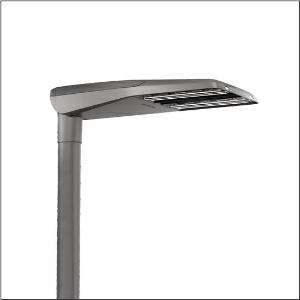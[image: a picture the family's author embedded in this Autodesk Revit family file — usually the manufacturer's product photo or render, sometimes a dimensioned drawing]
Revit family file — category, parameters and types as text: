
# Revit family: streetlight_sl_11_iq_midi___st1_0st0_5_5xc3j51g08me_56cc
name_source: partatom
category: Lighting Fixtures
units: mm (PartAtom-declared; Revit-internal decimal feet)

## family parameters
Cut with Voids When Loaded = No
Host = Face
Light Source = No
Part Type = Normal
Room Calculation Point = No
Round Connector Dimension = Use Diameter
Shared = No

## types (1)
- --- (1 x LED, 9460 lm, 63 W, 3000K)
    Apparent Load = 63 VA
    CIE Flux Codes = 35 68 96 100 100
    Color Rendering = 70
    Color Temperature = 3000K
    Default Elevation = 1800 mm
    Description = Streetlight SL 11 iQ midi, mast luminaire, primary light control with 3 zone facetted reflector, of plastic, silver coated, highly specular, primary optical cover: cover, of PMMA, transparent, light distribution: ST1.0ST0.5, light emission: direct distribution, primary light characteristic: asymmetric, installation type: post-top, side-entry, LED, High Power LED, rated luminous flux: 9.460lm, luminous efficacy: 150lm/W, light colour: 730, colour temperature: 3000K, control: Street-Remote, Auto-Match, Temp-Guard, Lumen-Switch, Night-Set, Smart-Wire, Light-Fading, Desk-Remote (wireless, voltage-free reading and setting of iQ features in the workshop via application-optimized NFC function/RFID function), optimised constant luminous flux control (CLO 2.0), pre-setting: linear dimming characteristic, with cable H07RN-F 5x 1.5mm², mains connection: 230..240V, AC, 50/60Hz, connection cable pre-assembled, cable length: 12,5m, start of lifetime: 63W, end of service life: 67W, reduction: 30W, luminaire housing, of diecast aluminium, powder-coated, Siteco® metallic grey (DB 702S), please order mast flange separately, inclination adjustable without tools: 0°, 5°, 10°, 15° (post-top) | 0°, -5°, -10°, -15° (side-entry), sealing non-destructively replaceable, multi-level sealing system, length: 780mm, width: 376mm, height: 118mm, mast flange for spigot size: 42mm (side-entry): 5XC10008XM4, 60/48mm (side-entry/post-top): 5XC10108XM2, 76/60mm (side-entry/post-top): 5XC10108XM1, equipment: Power, protection rating (complete): IP66, insulation class (complete): insulation class II (safety insulation), certification: CE, ENEC, VDE, impact resistance: IK09, permissible operating ambient temperature for outdoor applications: -25..+50°C, standard-compliant lighting for roads and squares, Environmental Product Declaration (EPD) tested and certified by an independent institute, packaging unit: 1 piece

Light Distribution: ST1.0ST0.5
    Height = 118 mm
    Lamp = 1 x LED
    Lamp Light Flux = 9460 lm
    Lamp Power = 63 W
    Lamp count = 1
    Length = 780 mm
    Luminous efficacy = 150 lm/W
    Manufacturer = Siteco
    ModVariant = No
    Model = 5XC3J51G08ME
    Number of Poles = 1
    OnlyDefault = Yes
    Power Factor = 1
    Product Name = Streetlight SL 11 iQ midi | ST1.0ST0.5
    Product group = mast luminaire | pylon top
    ProductGroupID = 6100
    Protection Class = Protection class II
    Protection Degree = IP 66
    RLX_Detail_Level = 1
    RLX_Emergency_Light_Flux = 0 lm
    RLX_Emergency_Type = 0
    RLX_Emergency_Type_DB = No
    RlxData = <blob elided: 70545 chars, md5=0e4ca75e>
    Socket = socket
    Standby Power = 0 W
    System Light Flux = 9460 lm
    System Power = 63 W
    Type Comments = factory setting: luminous flux: 100 % | dim-lin: 254 | 553 mA
    Type Image = l_1005960.jpg
    URL = http://relux.com
    VarID = @adj_008811
    Voltage = 0 V
    Weight = 0.00 kg
    Width = 376 mm

## geometry (parser evidence)
native form markers: Blend x4, Sweep x10
no freeform markers — native parametric forms only
